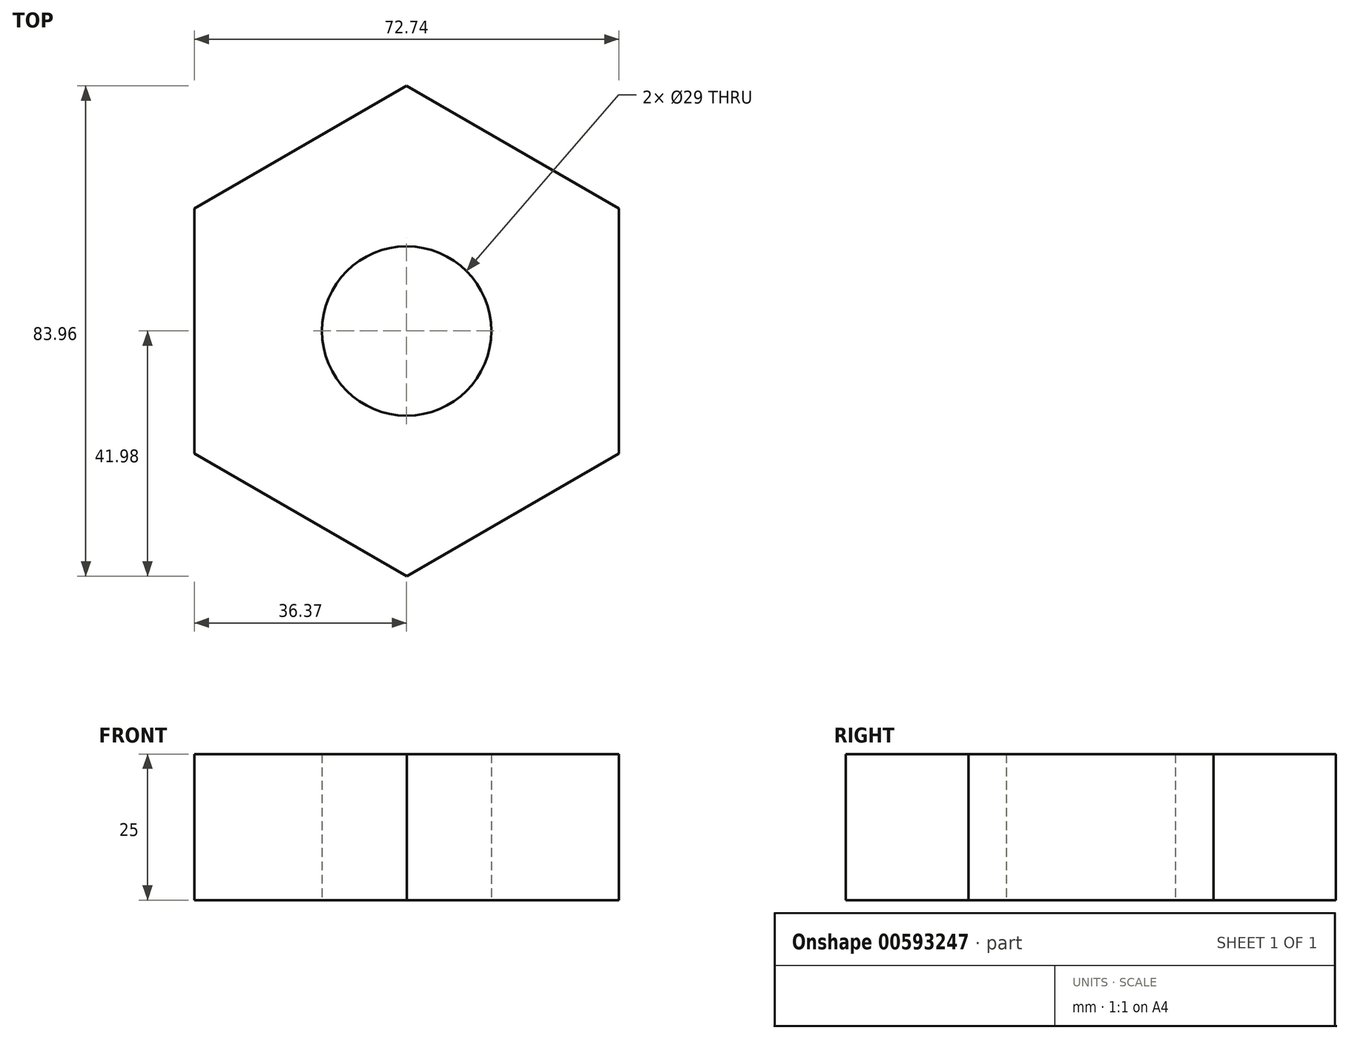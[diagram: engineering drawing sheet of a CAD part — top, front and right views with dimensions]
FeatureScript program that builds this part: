
annotation { "Feature Type Name" : "Feature", "Feature Type Description" : "" }
export const myFeature = defineFeature(function(context is Context, id is Id, definition is map)
    precondition{}
    {
        {
            var Q0;
            Q0=qCreatedBy(makeId("Top.planeOp"),FACE);
            var sketch = newSketch(context, id + "F0", { "sketchPlane" : qUnion([Q0])});
            skCircle(sketch, "E0.cCircle", {"center": v(0, 0) * mm, "radius": 36.36 * mm, "construction": true});
            skLineSegment(sketch, "E0.0", {"start": v(-0.02, 41.98) * mm, "end": v(36.35, 21.01) * mm});
            skLineSegment(sketch, "E0.1", {"start": v(36.35, 21.01) * mm, "end": v(36.37, -20.97) * mm});
            skLineSegment(sketch, "E0.2", {"start": v(36.37, -20.97) * mm, "end": v(0.02, -41.98) * mm});
            skLineSegment(sketch, "E0.3", {"start": v(0.02, -41.98) * mm, "end": v(-36.35, -21.01) * mm});
            skLineSegment(sketch, "E0.4", {"start": v(-36.35, -21.01) * mm, "end": v(-36.37, 20.97) * mm});
            skLineSegment(sketch, "E0.5", {"start": v(-36.37, 20.97) * mm, "end": v(-0.02, 41.98) * mm});
            skPoint(sketch, "E0.0.midPoint", {"position": v(18.16, 31.5) * mm});
            skCircle(sketch, "E1", {"center": v(0, 0) * mm, "radius": 14.5 * mm});
            skSolve(sketch);
        }
        {
            var Q0;
            Q0=makeQuery(id+"F0.imprint","IMPRINT",FACE,{"disambiguationData":[TD([[makeQuery(id+"F0.imprint","IMPRINT",EDGE,{"derivedFrom":sQuery(id+"F0.wireOp",EDGE,"E0.0")}),-1.0]])]});
            extrude(context, id + "F1", {"entities" : qUnion([Q0]), "depth" : 25 * mm, "offsetDistance" : 25 * mm});
        }
    });
